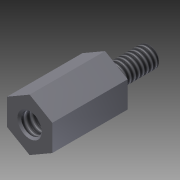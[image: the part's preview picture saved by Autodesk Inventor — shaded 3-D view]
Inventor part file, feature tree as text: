
AUTODESK INVENTOR PART (.ipt)
format: ipt  version: 2011 (Build 150239000, 239)  size: 110,080 bytes
history: native  units: in
note: dims shown in document units (in); Inventor stores cm internally (conversion verified against a paired STEP export)
features: sketch x5, chamfer x3, extrude x2, hole x1, thread x1, plane x1, revolve x1, other x1
ambient origin geometry x8: Origin, YZ Plane, XZ Plane, XY Plane, X Axis, Y Axis, Z Axis, Center Point
bodies: Solid1 (feature_tree)
feature tree (15):
  sketch  "Sketch1"  dims[d1=0.3125in d2=0.0in d3=0.1875in]
  extrude  "Hexagon1"  Depth=0.1875in
  sketch  "Sketch3"  dims[d12=0.1875in d13=0.0in d14=0.0078in d15=0.125in d16=45.0deg d17=0.0078in d18=0.125in d19=45.0deg d20=1.0in d21=0.0in d22=90.0deg]
  hole  "Hole1"  [1 undecoded]
  extrude  "Extrusion2"  Depth=0.0078in TaperAngle=45.0deg
  chamfer  "Chamfer1"  Distance=0.0078in Angle=45.0deg
  chamfer  "Chamfer2"  Distance=1.0in
  thread  "Thread1"  [1 undecoded]
  plane  "Work Plane1"
  revolve  "Revolution1"  Angle=45.0deg
  chamfer  "Chamfer3"  [1 undecoded]
  sketch  "Sketch2"  dims[d4=0.085in d5=0.5in d6=0.375in d7=0.25in d8=0.5635in d9=0.25in d10=0.8108in d11=0.085in]
  sketch  "Sketch4"  dims[d23=90.0deg d24=0.0078in d25=0.125in d26=45.0deg]
  other  "Work Axis1"
  sketch  "Sketch5"
note: 3 required parameter values undecoded (feature->parameter linkage not recoverable at this tier; creation-order binding heuristic only, values carry confidence <= 0.55)
